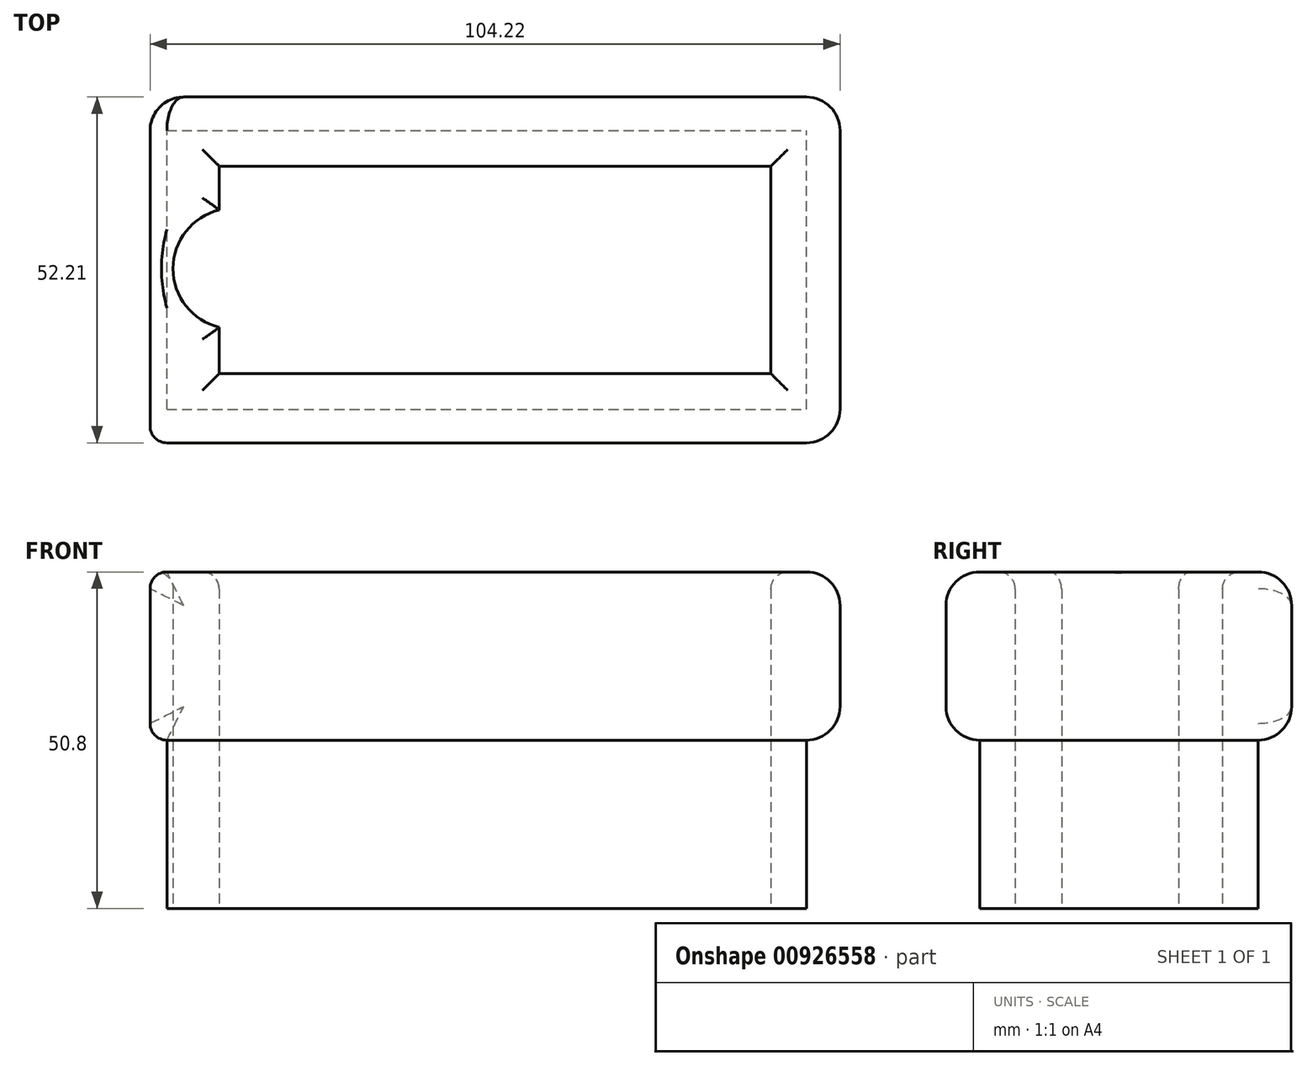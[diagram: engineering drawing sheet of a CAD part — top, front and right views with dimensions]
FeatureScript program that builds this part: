
annotation { "Feature Type Name" : "Feature", "Feature Type Description" : "" }
export const myFeature = defineFeature(function(context is Context, id is Id, definition is map)
    precondition{}
    {
        {
            var Q0;
            Q0=qCreatedBy(makeId("Top.planeOp"),FACE);
            var sketch = newSketch(context, id + "F0", { "sketchPlane" : qUnion([Q0])});
            skLineSegment(sketch, "E0.bottom", {"start": v(0, 0) * mm, "end": v(104.22, 0) * mm});
            skLineSegment(sketch, "E0.top", {"start": v(0, 52.2) * mm, "end": v(104.22, 52.2) * mm});
            skLineSegment(sketch, "E0.left", {"start": v(0, 0) * mm, "end": v(0, 52.2) * mm});
            skLineSegment(sketch, "E0.right", {"start": v(104.22, 0) * mm, "end": v(104.22, 52.2) * mm});
            skCircle(sketch, "E1", {"center": v(12.57, 26.3) * mm, "radius": 9.1 * mm});
            skLineSegment(sketch, "E2.0", {"start": v(10.44, 41.77) * mm, "end": v(93.78, 41.77) * mm});
            skLineSegment(sketch, "E2.1", {"start": v(10.44, 10.44) * mm, "end": v(10.44, 41.77) * mm});
            skLineSegment(sketch, "E2.2", {"start": v(10.44, 10.44) * mm, "end": v(93.78, 10.44) * mm});
            skLineSegment(sketch, "E2.3", {"start": v(93.78, 10.44) * mm, "end": v(93.78, 41.77) * mm});
            skSolve(sketch);
        }
        {
            var Q0;
            Q0=makeQuery(id+"F0.imprint","IMPRINT",FACE,{"disambiguationData":[TD([[makeQuery(id+"F0.imprint","IMPRINT",EDGE,{"derivedFrom":sQuery(id+"F0.wireOp",EDGE,"E0.bottom")}),1.0]])]});
            extrude(context, id + "F1", {"entities" : qUnion([Q0]), "depth" : 25.4 * mm, "offsetDistance" : 25.4 * mm});
        }
        {
            var Q0;
            Q0=makeQuery(id+"F1.opExtrude","SWEPT_EDGE",EDGE,{"disambiguationData":[OSD([sQuery(id+"F0.wireOp",EDGE,"E0.bottom"),sQuery(id+"F0.wireOp",EDGE,"E0.right")])]});
            var Q1;
            Q1=makeQuery(id+"F1.opExtrude","SWEPT_FACE",FACE,{"disambiguationData":[OSD([sQuery(id+"F0.wireOp",EDGE,"E0.right")])]});
            var Q2;
            Q2=makeQuery(id+"F1.opExtrude","CAP_EDGE",EDGE,{"disambiguationData":[OSD([sQuery(id+"F0.wireOp",EDGE,"E0.bottom")])],"isStart":false});
            var Q3;
            Q3=makeQuery(id+"F1.opExtrude","CAP_EDGE",EDGE,{"disambiguationData":[OSD([sQuery(id+"F0.wireOp",EDGE,"E0.bottom")])],"isStart":true});
            var Q4;
            Q4=makeQuery(id+"F1.opExtrude","CAP_EDGE",EDGE,{"disambiguationData":[OSD([sQuery(id+"F0.wireOp",EDGE,"E0.top")])],"isStart":false});
            var Q5;
            Q5=makeQuery(id+"F1.opExtrude","SWEPT_FACE",FACE,{"disambiguationData":[OSD([sQuery(id+"F0.wireOp",EDGE,"E0.top")])]});
            var Q6;
            Q6=makeQuery(id+"F1.opExtrude","SWEPT_EDGE",EDGE,{"disambiguationData":[OSD([sQuery(id+"F0.wireOp",EDGE,"E0.top"),sQuery(id+"F0.wireOp",EDGE,"E0.right")])]});
            fillet(context, id + "F2", {"entities" : qUnion([Q0, Q1, Q2, Q3, Q4, Q5, Q6]), "radius" : 5.08 * mm, "tangentPropagation" : true, "allowEdgeOverflow" : false});
        }
        {
            var Q0;
            {var subQ0=sQuery(id+"F0.wireOp",EDGE,"E0.top");Q0=makeQuery(id+"F2.opFillet","BLEND_EDGE",EDGE,{"blendedFrom":[makeQuery(id+"F1.opExtrude","CAP_EDGE",EDGE,{"disambiguationData":[OSD([subQ0])],"isStart":false}),makeQuery(id+"F1.opExtrude","CAP_FACE",FACE,{"disambiguationData":[OSD([sQuery(id+"F0.wireOp",EDGE,"E0.bottom"),subQ0,sQuery(id+"F0.wireOp",EDGE,"E0.left"),sQuery(id+"F0.wireOp",EDGE,"E0.right"),sQuery(id+"F0.wireOp",EDGE,"E1"),sQuery(id+"F0.wireOp",EDGE,"E2.0"),sQuery(id+"F0.wireOp",EDGE,"E2.1"),sQuery(id+"F0.wireOp",EDGE,"E2.2"),sQuery(id+"F0.wireOp",EDGE,"E2.3")])],"isStart":false})],"blendedInto":[makeQuery(id+"F1.opExtrude","CAP_FACE",FACE,{"disambiguationData":[OSD([sQuery(id+"F0.wireOp",EDGE,"E0.bottom"),subQ0,sQuery(id+"F0.wireOp",EDGE,"E0.left"),sQuery(id+"F0.wireOp",EDGE,"E0.right"),sQuery(id+"F0.wireOp",EDGE,"E1"),sQuery(id+"F0.wireOp",EDGE,"E2.0"),sQuery(id+"F0.wireOp",EDGE,"E2.1"),sQuery(id+"F0.wireOp",EDGE,"E2.2"),sQuery(id+"F0.wireOp",EDGE,"E2.3")])],"isStart":false})]});}
            var Q1;
            {var subQ0=sQuery(id+"F0.wireOp",EDGE,"E0.top");Q1=makeQuery(id+"F2.opFillet","BLEND_EDGE",EDGE,{"blendedFrom":[makeQuery(id+"F1.opExtrude","CAP_EDGE",EDGE,{"disambiguationData":[OSD([subQ0])],"isStart":false}),makeQuery(id+"F1.opExtrude","SWEPT_FACE",FACE,{"disambiguationData":[OSD([subQ0])]})],"blendedInto":[makeQuery(id+"F1.opExtrude","SWEPT_FACE",FACE,{"disambiguationData":[OSD([subQ0])]})]});}
            var Q2;
            {var subQ0=sQuery(id+"F0.wireOp",EDGE,"E0.bottom");Q2=makeQuery(id+"F2.opFillet","BLEND_EDGE",EDGE,{"blendedFrom":[makeQuery(id+"F1.opExtrude","CAP_EDGE",EDGE,{"disambiguationData":[OSD([subQ0])],"isStart":false}),makeQuery(id+"F1.opExtrude","SWEPT_FACE",FACE,{"disambiguationData":[OSD([subQ0])]})],"blendedInto":[makeQuery(id+"F1.opExtrude","SWEPT_FACE",FACE,{"disambiguationData":[OSD([subQ0])]})]});}
            var Q3;
            Q3=makeQuery(id+"F1.opExtrude","CAP_EDGE",EDGE,{"disambiguationData":[OSD([sQuery(id+"F0.wireOp",EDGE,"E2.2")])],"isStart":false});
            var Q4;
            {var subQ0=sQuery(id+"F0.wireOp",EDGE,"E0.right");Q4=makeQuery(id+"F2.opFillet","BLEND_EDGE",EDGE,{"blendedFrom":[makeQuery(id+"F1.opExtrude","CAP_EDGE",EDGE,{"disambiguationData":[OSD([subQ0])],"isStart":false}),makeQuery(id+"F1.opExtrude","SWEPT_FACE",FACE,{"disambiguationData":[OSD([subQ0])]})],"blendedInto":[makeQuery(id+"F1.opExtrude","SWEPT_FACE",FACE,{"disambiguationData":[OSD([subQ0])]})]});}
            var Q5;
            Q5=makeQuery(id+"F1.opExtrude","CAP_FACE",FACE,{"disambiguationData":[OSD([sQuery(id+"F0.wireOp",EDGE,"E0.bottom"),sQuery(id+"F0.wireOp",EDGE,"E0.top"),sQuery(id+"F0.wireOp",EDGE,"E0.left"),sQuery(id+"F0.wireOp",EDGE,"E0.right"),sQuery(id+"F0.wireOp",EDGE,"E1"),sQuery(id+"F0.wireOp",EDGE,"E2.0"),sQuery(id+"F0.wireOp",EDGE,"E2.1"),sQuery(id+"F0.wireOp",EDGE,"E2.2"),sQuery(id+"F0.wireOp",EDGE,"E2.3")])],"isStart":false});
            fillet(context, id + "F3", {"entities" : qUnion([Q0, Q1, Q2, Q3, Q4, Q5]), "radius" : 2.54 * mm, "tangentPropagation" : true, "allowEdgeOverflow" : false});
        }
        {
            var Q0;
            Q0=makeQuery(id+"F1.opExtrude","CAP_FACE",FACE,{"disambiguationData":[OSD([sQuery(id+"F0.wireOp",EDGE,"E0.bottom"),sQuery(id+"F0.wireOp",EDGE,"E0.top"),sQuery(id+"F0.wireOp",EDGE,"E0.left"),sQuery(id+"F0.wireOp",EDGE,"E0.right"),sQuery(id+"F0.wireOp",EDGE,"E1"),sQuery(id+"F0.wireOp",EDGE,"E2.0"),sQuery(id+"F0.wireOp",EDGE,"E2.1"),sQuery(id+"F0.wireOp",EDGE,"E2.2"),sQuery(id+"F0.wireOp",EDGE,"E2.3")])],"isStart":false});
            extrude(context, id + "F4", {"entities" : qUnion([Q0]), "operationType" : NewBodyOperationType.ADD, "oppositeDirection" : true, "depth" : 1.15 * mm, "offsetDistance" : 25.4 * mm});
        }
        {
            var Q0;
            Q0=makeQuery(id+"F1.opExtrude","CAP_FACE",FACE,{"disambiguationData":[OSD([sQuery(id+"F0.wireOp",EDGE,"E0.bottom"),sQuery(id+"F0.wireOp",EDGE,"E0.top"),sQuery(id+"F0.wireOp",EDGE,"E0.left"),sQuery(id+"F0.wireOp",EDGE,"E0.right"),sQuery(id+"F0.wireOp",EDGE,"E1"),sQuery(id+"F0.wireOp",EDGE,"E2.0"),sQuery(id+"F0.wireOp",EDGE,"E2.1"),sQuery(id+"F0.wireOp",EDGE,"E2.2"),sQuery(id+"F0.wireOp",EDGE,"E2.3")])],"isStart":true});
            var sketch = newSketch(context, id + "F5", { "sketchPlane" : qUnion([Q0])});
            skSolve(sketch);
        }
        {
            var Q0;
            {var subQ2=sQuery(id+"F0.wireOp",EDGE,"E1");Q0=makeQuery(id+"F5.imprint","IMPRINT",FACE,{"disambiguationData":[TD([[makeQuery(id+"F5.imprint","IMPRINT",EDGE,{"derivedFrom":makeQuery(id+"F1.opExtrude","CAP_EDGE",EDGE,{"disambiguationData":[OSD([subQ2])],"isStart":true})}),1.0]])]});}
            var Q1;
            Q1=makeQuery(id+"F1.opExtrude","CAP_FACE",FACE,{"disambiguationData":[OSD([sQuery(id+"F0.wireOp",EDGE,"E0.bottom"),sQuery(id+"F0.wireOp",EDGE,"E0.top"),sQuery(id+"F0.wireOp",EDGE,"E0.left"),sQuery(id+"F0.wireOp",EDGE,"E0.right"),sQuery(id+"F0.wireOp",EDGE,"E1"),sQuery(id+"F0.wireOp",EDGE,"E2.0"),sQuery(id+"F0.wireOp",EDGE,"E2.1"),sQuery(id+"F0.wireOp",EDGE,"E2.2"),sQuery(id+"F0.wireOp",EDGE,"E2.3")])],"isStart":true});
            var Q2;
            Q2=makeQuery(id+"F1.opExtrude","CAP_FACE",FACE,{"disambiguationData":[OSD([sQuery(id+"F0.wireOp",EDGE,"E0.bottom"),sQuery(id+"F0.wireOp",EDGE,"E0.top"),sQuery(id+"F0.wireOp",EDGE,"E0.left"),sQuery(id+"F0.wireOp",EDGE,"E0.right"),sQuery(id+"F0.wireOp",EDGE,"E1"),sQuery(id+"F0.wireOp",EDGE,"E2.0"),sQuery(id+"F0.wireOp",EDGE,"E2.1"),sQuery(id+"F0.wireOp",EDGE,"E2.2"),sQuery(id+"F0.wireOp",EDGE,"E2.3")])],"isStart":false});
            extrude(context, id + "F6", {"entities" : qUnion([Q0, Q1, Q2]), "operationType" : NewBodyOperationType.ADD, "depth" : 25.4 * mm, "offsetDistance" : 25.4 * mm});
        }
    });
